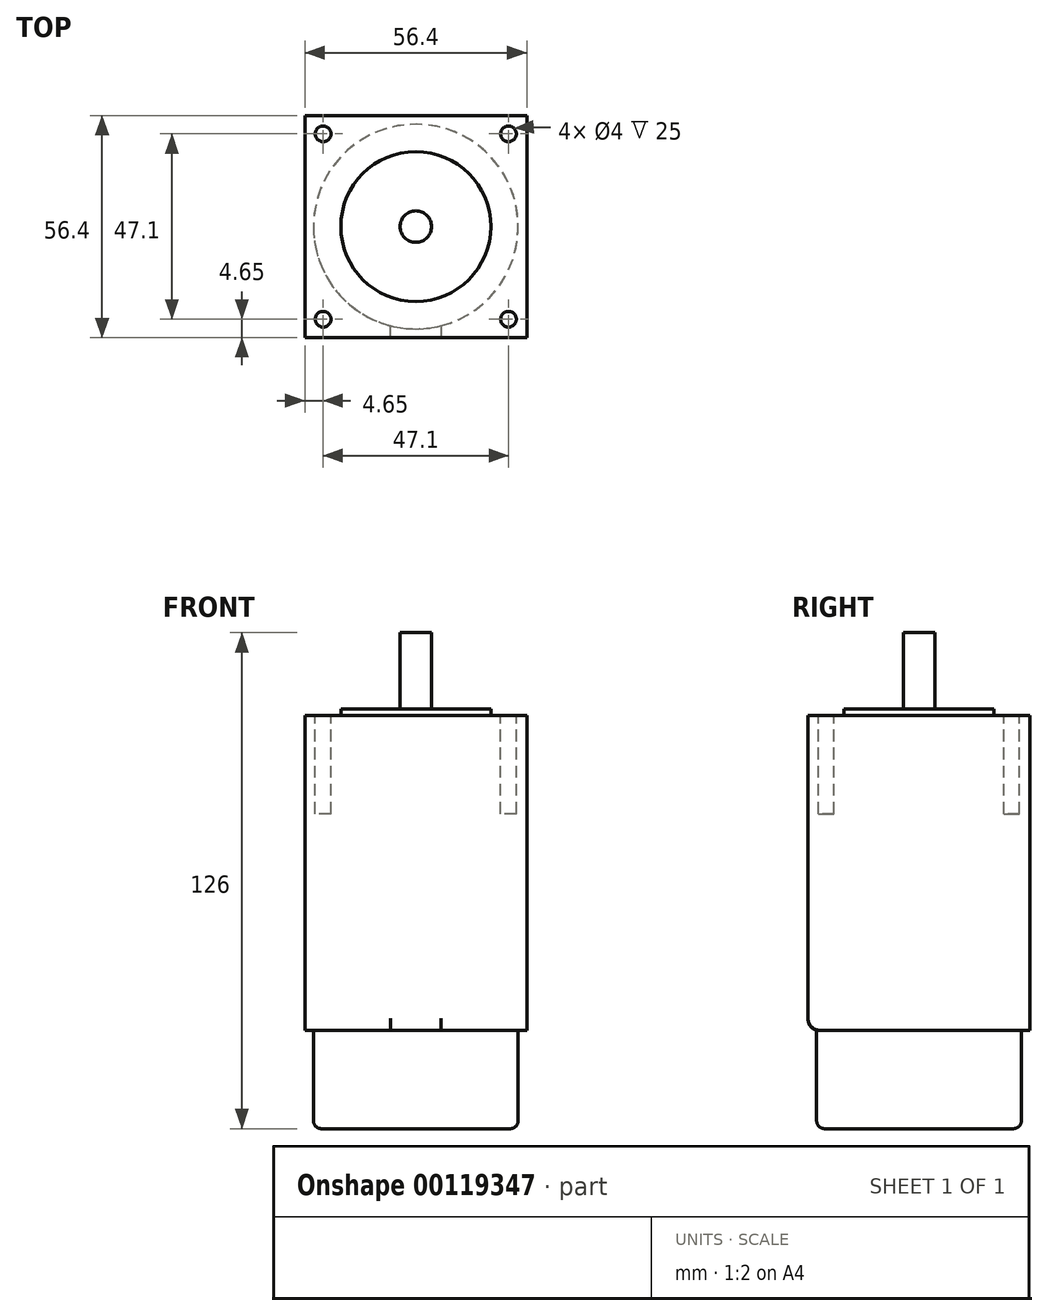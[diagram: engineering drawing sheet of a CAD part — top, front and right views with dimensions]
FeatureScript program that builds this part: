
annotation { "Feature Type Name" : "Feature", "Feature Type Description" : "" }
export const myFeature = defineFeature(function(context is Context, id is Id, definition is map)
    precondition{}
    {
        {
            var Q0;
            Q0=qCreatedBy(makeId("Top.planeOp"),FACE);
            var sketch = newSketch(context, id + "F0", { "sketchPlane" : qUnion([Q0])});
            skLineSegment(sketch, "E0.bottom", {"start": v(28.2, 28.2) * mm, "end": v(-28.2, 28.2) * mm});
            skLineSegment(sketch, "E0.top", {"start": v(28.2, -28.2) * mm, "end": v(-28.2, -28.2) * mm});
            skLineSegment(sketch, "E0.left", {"start": v(28.2, 28.2) * mm, "end": v(28.2, -28.2) * mm});
            skLineSegment(sketch, "E0.right", {"start": v(-28.2, 28.2) * mm, "end": v(-28.2, -28.2) * mm});
            skPoint(sketch, "E0.middle", {"position": v(0, 0) * mm});
            skSolve(sketch);
        }
        {
            var Q0;
            Q0 = qSketchRegion(id + "F0", true);
            extrude(context, id + "F1", {"entities" : qUnion([Q0]), "depth" : 80 * mm});
        }
        {
            var Q0;
            Q0=makeQuery(id+"F1.opExtrude","CAP_FACE",FACE,{"disambiguationData":[OSD([sQuery(id+"F0.wireOp",EDGE,"E0.bottom"),sQuery(id+"F0.wireOp",EDGE,"E0.top"),sQuery(id+"F0.wireOp",EDGE,"E0.left"),sQuery(id+"F0.wireOp",EDGE,"E0.right")])],"isStart":false});
            var sketch = newSketch(context, id + "F2", { "sketchPlane" : qUnion([Q0])});
            skCircle(sketch, "E1", {"center": v(0, 0) * mm, "radius": 19.05 * mm});
            skSolve(sketch);
        }
        {
            var Q0;
            Q0 = qSketchRegion(id + "F2", true);
            extrude(context, id + "F3", {"entities" : qUnion([Q0]), "operationType" : NewBodyOperationType.ADD, "depth" : 1.6 * mm});
        }
        {
            var Q0;
            Q0=makeQuery(id+"F3.opExtrude","CAP_FACE",FACE,{"disambiguationData":[OSD([sQuery(id+"F2.wireOp",EDGE,"E1")])],"isStart":false});
            var sketch = newSketch(context, id + "F4", { "sketchPlane" : qUnion([Q0])});
            skCircle(sketch, "E2", {"center": v(0, 0) * mm, "radius": 4 * mm});
            skSolve(sketch);
        }
        {
            var Q0;
            Q0 = qSketchRegion(id + "F4", true);
            extrude(context, id + "F5", {"entities" : qUnion([Q0]), "operationType" : NewBodyOperationType.ADD, "depth" : 19.4 * mm});
        }
        {
            var Q0;
            Q0=makeQuery(id+"F1.opExtrude","CAP_FACE",FACE,{"disambiguationData":[OSD([sQuery(id+"F0.wireOp",EDGE,"E0.bottom"),sQuery(id+"F0.wireOp",EDGE,"E0.top"),sQuery(id+"F0.wireOp",EDGE,"E0.left"),sQuery(id+"F0.wireOp",EDGE,"E0.right")])],"isStart":false});
            var sketch = newSketch(context, id + "F6", { "sketchPlane" : qUnion([Q0])});
            skCircle(sketch, "E3", {"center": v(23.55, 23.55) * mm, "radius": 2 * mm});
            skCircle(sketch, "E4.MirrorC", {"center": v(-23.55, 23.55) * mm, "radius": 2 * mm});
            skCircle(sketch, "E5.MirrorC", {"center": v(-23.55, -23.55) * mm, "radius": 2 * mm});
            skCircle(sketch, "E6.MirrorC", {"center": v(23.55, -23.55) * mm, "radius": 2 * mm});
            skSolve(sketch);
        }
        {
            var Q0;
            Q0 = qSketchRegion(id + "F6", true);
            extrude(context, id + "F7", {"entities" : qUnion([Q0]), "operationType" : NewBodyOperationType.REMOVE, "oppositeDirection" : true, "depth" : 25 * mm});
        }
        {
            var Q0;
            Q0=makeQuery(id+"F1.opExtrude","CAP_FACE",FACE,{"disambiguationData":[OSD([sQuery(id+"F0.wireOp",EDGE,"E0.bottom"),sQuery(id+"F0.wireOp",EDGE,"E0.top"),sQuery(id+"F0.wireOp",EDGE,"E0.left"),sQuery(id+"F0.wireOp",EDGE,"E0.right")])],"isStart":true});
            var sketch = newSketch(context, id + "F8", { "sketchPlane" : qUnion([Q0])});
            skCircle(sketch, "E7", {"center": v(0, 0) * mm, "radius": 26 * mm});
            skSolve(sketch);
        }
        {
            var Q0;
            Q0 = qSketchRegion(id + "F8", true);
            extrude(context, id + "F9", {"entities" : qUnion([Q0]), "operationType" : NewBodyOperationType.ADD, "depth" : 25 * mm});
        }
        {
            var Q0;
            Q0=makeQuery(id+"F1.opExtrude","CAP_EDGE",EDGE,{"disambiguationData":[OSD([sQuery(id+"F0.wireOp",EDGE,"E0.top")])],"isStart":true});
            fillet(context, id + "F10", {"entities" : qUnion([Q0]), "radius" : 3 * mm, "tangentPropagation" : true, "allowEdgeOverflow" : false});
        }
        {
            var Q0;
            Q0=makeQuery(id+"F9.opExtrude","CAP_EDGE",EDGE,{"disambiguationData":[OSD([sQuery(id+"F8.wireOp",EDGE,"E7")])],"isStart":false});
            fillet(context, id + "F11", {"entities" : qUnion([Q0]), "radius" : 2 * mm, "tangentPropagation" : true, "allowEdgeOverflow" : false});
        }
    });
